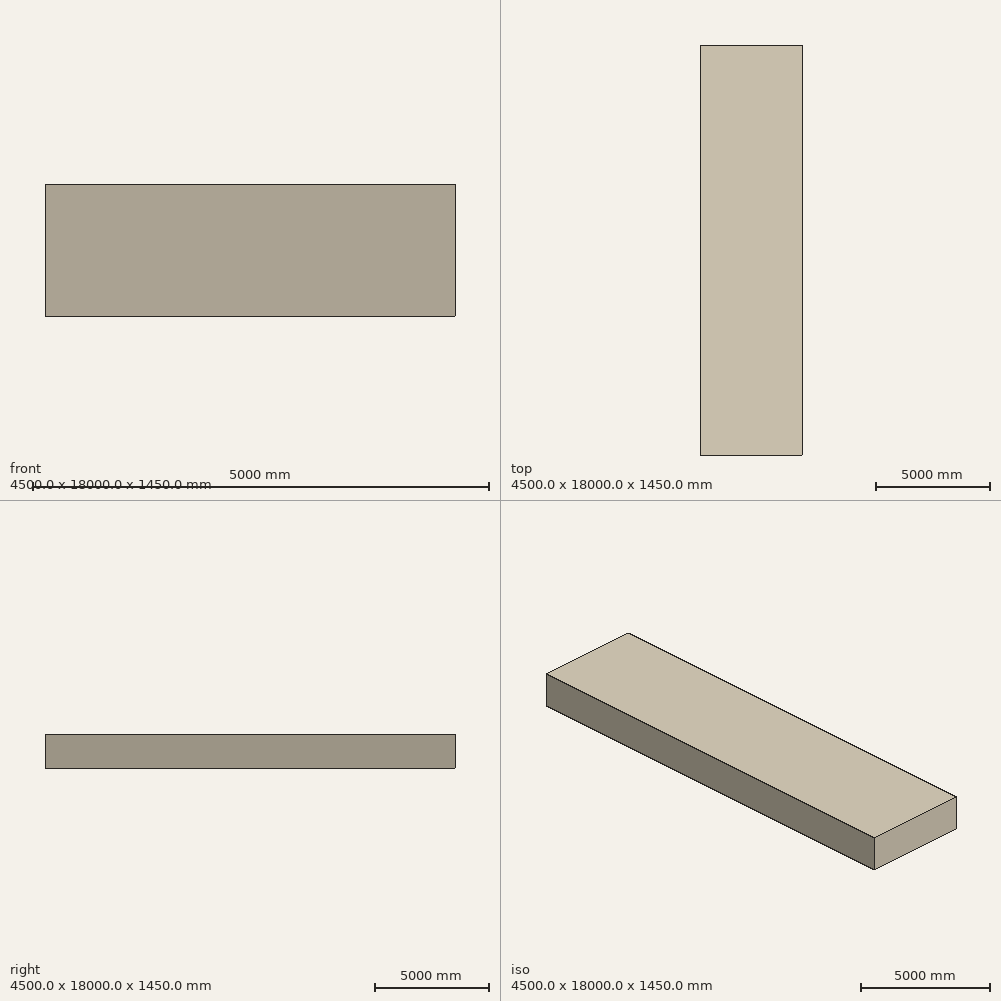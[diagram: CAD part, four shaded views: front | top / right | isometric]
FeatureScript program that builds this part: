
annotation { "Feature Type Name" : "Feature", "Feature Type Description" : "" }
export const myFeature = defineFeature(function(context is Context, id is Id, definition is map)
    precondition{}
    {
        {
            var Q0;
            Q0=qCreatedBy(makeId("Front.planeOp"),FACE);
            var sketch = newSketch(context, id + "F0", { "sketchPlane" : qUnion([Q0])});
            skLineSegment(sketch, "E0.bottom", {"start": v(0, 0) * mm, "end": v(-4500, 0) * mm});
            skLineSegment(sketch, "E0.top", {"start": v(0, -1450) * mm, "end": v(-4500, -1450) * mm});
            skLineSegment(sketch, "E0.left", {"start": v(0, 0) * mm, "end": v(0, -1450) * mm});
            skLineSegment(sketch, "E0.right", {"start": v(-4500, 0) * mm, "end": v(-4500, -1450) * mm});
            skSolve(sketch);
        }
        {
            var Q0;
            Q0=makeQuery(id+"F0.imprint","IMPRINT",FACE,{"disambiguationData":[TD([[makeQuery(id+"F0.imprint","IMPRINT",EDGE,{"derivedFrom":sQuery(id+"F0.wireOp",EDGE,"E0.bottom")}),1.0]])]});
            extrude(context, id + "F1", {"entities" : qUnion([Q0]), "oppositeDirection" : true, "depth" : 18000 * mm, "offsetDistance" : 25 * mm});
        }
    });
